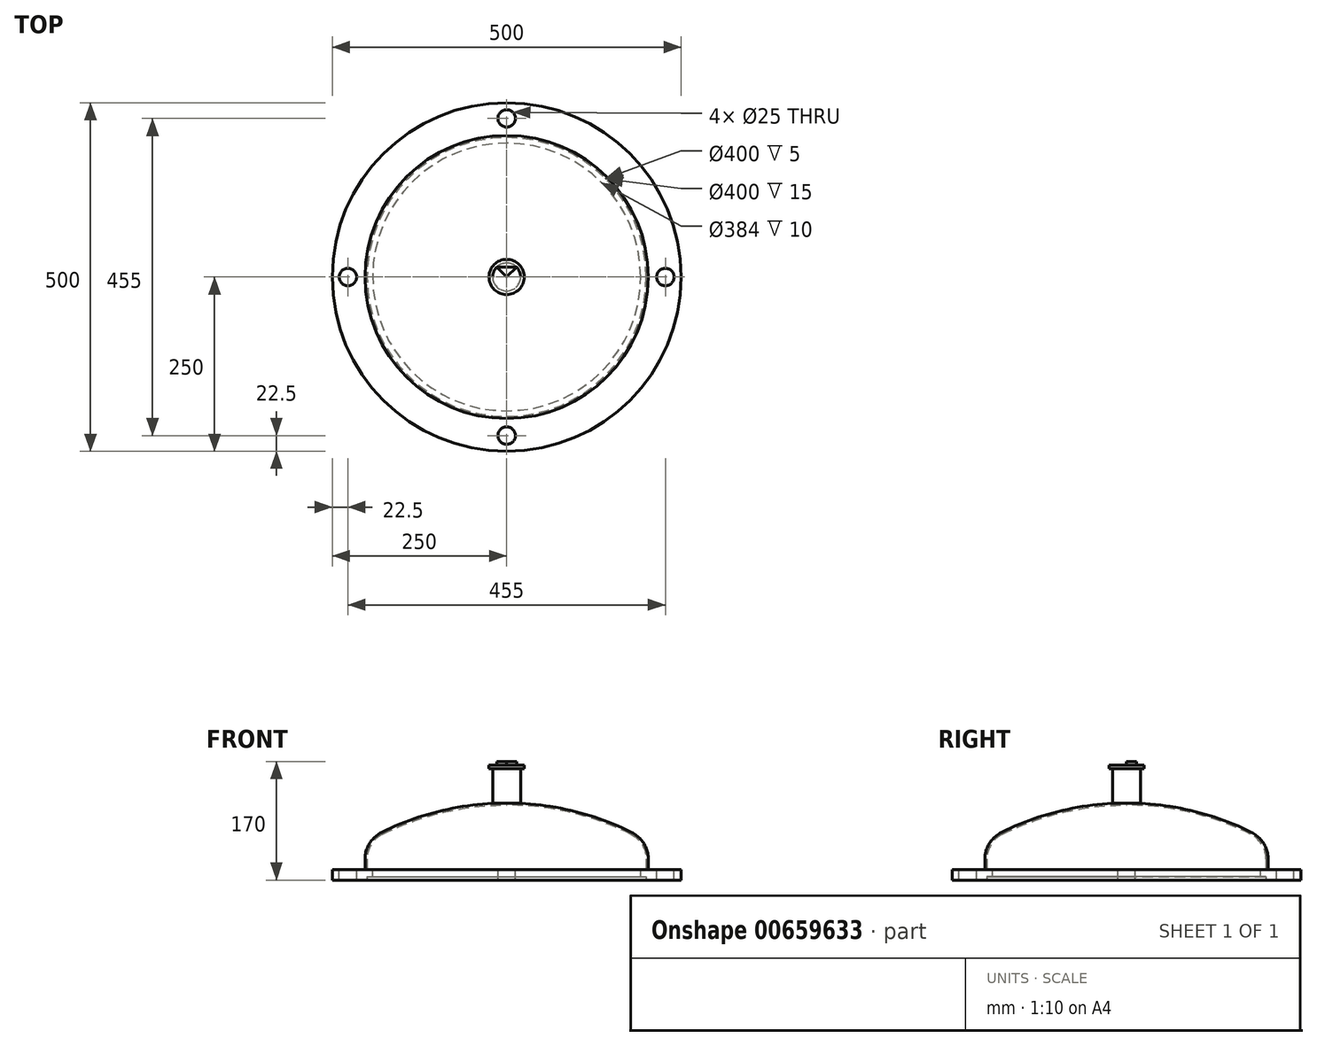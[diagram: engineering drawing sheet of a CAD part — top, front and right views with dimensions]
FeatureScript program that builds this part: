
annotation { "Feature Type Name" : "Feature", "Feature Type Description" : "" }
export const myFeature = defineFeature(function(context is Context, id is Id, definition is map)
    precondition{}
    {
        {
            var Q0;
            Q0=qCreatedBy(makeId("Front.planeOp"),FACE);
            var sketch = newSketch(context, id + "F0", { "sketchPlane" : qUnion([Q0])});
            skLineSegment(sketch, "E0", {"start": v(200, 0) * mm, "end": v(203, 0) * mm});
            skLineSegment(sketch, "E1", {"start": v(203, 0) * mm, "end": v(203, 20) * mm});
            skLineSegment(sketch, "E2", {"start": v(200, 0) * mm, "end": v(200, 20) * mm});
            skArc(sketch, "E3", {"start": v(200, 20) * mm, "mid": v(194, 41.07) * mm, "end": v(177.8, 55.82) * mm});
            skArc(sketch, "E4", {"start": v(177.8, 55.82) * mm, "mid": v(91.32, 87) * mm, "end": v(0, 97.6) * mm});
            skArc(sketch, "E5.0", {"start": v(179.13, 58.5) * mm, "mid": v(92, 89.92) * mm, "end": v(0, 100.6) * mm});
            skArc(sketch, "E5.1", {"start": v(203, 20) * mm, "mid": v(196.55, 42.65) * mm, "end": v(179.13, 58.5) * mm});
            skLineSegment(sketch, "E6", {"start": v(0, 97.6) * mm, "end": v(0, 100.6) * mm});
            skSolve(sketch);
        }
        {
            var Q0;
            Q0=qSketchRegion(id+"F0",true);
            var Q1;
            Q1=sQuery(id+"F0.wireOp",EDGE,"E6");
            revolve(context, id + "F1", {"entities" : qUnion([Q0]), "axis" : qUnion([Q1]), "revolveType" : RevolveType.FULL});
        }
        {
            var Q0;
            Q0=makeQuery(id+"F1.opRevolve","SWEPT_FACE",FACE,{"disambiguationData":[OSD([sQuery(id+"F0.wireOp",EDGE,"E0")])]});
            var sketch = newSketch(context, id + "F2", { "sketchPlane" : qUnion([Q0])});
            skCircle(sketch, "E7", {"center": v(0, 0) * mm, "radius": 250 * mm});
            skCircle(sketch, "E8", {"center": v(0, 0) * mm, "radius": 192 * mm});
            skSolve(sketch);
        }
        {
            var Q0;
            Q0=qSketchRegion(id+"F2",true);
            extrude(context, id + "F3", {"entities" : qUnion([Q0]), "operationType" : NewBodyOperationType.ADD, "depth" : 10 * mm, "offsetDistance" : 25 * mm, "hasSecondDirection" : true, "secondDirectionOppositeDirection" : true, "secondDirectionDepth" : 5 * mm});
        }
        {
            var Q0;
            Q0=qCreatedBy(makeId("Top.planeOp"),FACE);
            cPlane(context, id + "F4", {"entities" : qUnion([Q0]), "cplaneType" : CPlaneType.OFFSET, "offset" : 150 * mm, "width" : 150 * mm, "height" : 150 * mm});
        }
        {
            var Q0;
            Q0=qCreatedBy(id+"F4.planeOp",FACE);
            var sketch = newSketch(context, id + "F5", { "sketchPlane" : qUnion([Q0])});
            skCircle(sketch, "E9", {"center": v(0, 0) * mm, "radius": 20 * mm});
            skSolve(sketch);
        }
        {
            var Q0;
            Q0=qSketchRegion(id+"F5",true);
            extrude(context, id + "F6", {"entities" : qUnion([Q0]), "operationType" : NewBodyOperationType.ADD, "endBound" : BoundingType.UP_TO_NEXT, "oppositeDirection" : true, "depth" : 25 * mm, "offsetDistance" : 25 * mm});
        }
        {
            var Q0;
            Q0=makeQuery(id+"F6.opExtrude","CAP_FACE",FACE,{"disambiguationData":[OSD([sQuery(id+"F5.wireOp",EDGE,"E9")])],"isStart":true});
            var sketch = newSketch(context, id + "F7", { "sketchPlane" : qUnion([Q0])});
            skCircle(sketch, "E10", {"center": v(0, 0) * mm, "radius": 25.25 * mm});
            skSolve(sketch);
        }
        {
            var Q0;
            Q0=qSketchRegion(id+"F7",true);
            extrude(context, id + "F8", {"entities" : qUnion([Q0]), "operationType" : NewBodyOperationType.ADD, "depth" : 5 * mm, "offsetDistance" : 25 * mm});
        }
        {
            var Q0;
            Q0=makeQuery(id+"F8.opExtrude","CAP_FACE",FACE,{"disambiguationData":[OSD([sQuery(id+"F7.wireOp",EDGE,"E10")])],"isStart":false});
            var sketch = newSketch(context, id + "F9", { "sketchPlane" : qUnion([Q0])});
            skLineSegment(sketch, "E11", {"start": v(0, 0) * mm, "end": v(14.14, 14.14) * mm});
            skLineSegment(sketch, "E12", {"start": v(0, 0) * mm, "end": v(-14.14, 14.14) * mm});
            skLineSegment(sketch, "E13", {"start": v(0, 0) * mm, "end": v(12, 0) * mm, "construction": true});
            skLineSegment(sketch, "E14", {"start": v(-14.14, 14.14) * mm, "end": v(14.14, 14.14) * mm});
            skSolve(sketch);
        }
        {
            var Q0;
            Q0=qSketchRegion(id+"F9",true);
            extrude(context, id + "F10", {"entities" : qUnion([Q0]), "operationType" : NewBodyOperationType.ADD, "depth" : 5 * mm, "offsetDistance" : 25 * mm});
        }
        {
            var Q0;
            Q0=makeQuery(id+"F3.opExtrude","CAP_FACE",FACE,{"disambiguationData":[OSD([sQuery(id+"F2.wireOp",EDGE,"E7"),sQuery(id+"F2.wireOp",EDGE,"E8")])],"isStart":true});
            var sketch = newSketch(context, id + "F11", { "sketchPlane" : qUnion([Q0])});
            skCircle(sketch, "E15", {"center": v(227.5, 0) * mm, "radius": 12.5 * mm});
            skCircle(sketch, "E16.1.0", {"center": v(0, 227.5) * mm, "radius": 12.5 * mm});
            skCircle(sketch, "E16.2.0", {"center": v(-227.5, 0) * mm, "radius": 12.5 * mm});
            skCircle(sketch, "E16.3.0", {"center": v(0, -227.5) * mm, "radius": 12.5 * mm});
            skPoint(sketch, "E16.center", {"position": v(0, 0) * mm});
            skSolve(sketch);
        }
        {
            var Q0;
            Q0=qSketchRegion(id+"F11",true);
            extrude(context, id + "F12", {"entities" : qUnion([Q0]), "operationType" : NewBodyOperationType.REMOVE, "oppositeDirection" : true, "depth" : 20 * mm, "offsetDistance" : 25 * mm});
        }
        {
            var Q0;
            Q0=makeQuery(id+"F3.opExtrude","CAP_FACE",FACE,{"disambiguationData":[OSD([sQuery(id+"F2.wireOp",EDGE,"E7"),sQuery(id+"F2.wireOp",EDGE,"E8")])],"isStart":false});
            var sketch = newSketch(context, id + "F13", { "sketchPlane" : qUnion([Q0])});
            skCircle(sketch, "E17", {"center": v(0, 0) * mm, "radius": 200 * mm});
            skSolve(sketch);
        }
        {
            var Q0;
            Q0 = qSketchRegion(id + "F13", true);
            extrude(context, id + "F14", {"entities" : qUnion([Q0]), "operationType" : NewBodyOperationType.REMOVE, "oppositeDirection" : true, "depth" : 5 * mm, "offsetDistance" : 25 * mm});
        }
    });
